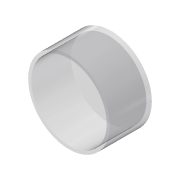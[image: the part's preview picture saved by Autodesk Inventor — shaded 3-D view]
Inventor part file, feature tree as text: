
AUTODESK INVENTOR PART (.ipt)
format: ipt  version: 2019.4 (Build 234330000, 330)  size: 91,136 bytes
history: native  units: mm
features: extrude x2, sketch x2, projected_geometry x1
ambient origin geometry x8: Origin, YZ Plane, XZ Plane, XY Plane, X Axis, Y Axis, Z Axis, Center Point
bodies: Solid1 (feature_tree)
feature tree (5):
  extrude  "Extrusion1"  Depth=18.0mm TaperAngle=0.0deg
  extrude  "Extrusion2"  [1 undecoded]
  sketch  "Sketch1"  dims[d0=35.0mm d1=18.0mm d2=0.0mm]
  sketch  "Sketch2"  dims[d3=17.0mm d4=0.0mm]
  projected_geometry  "Projected Loop1"
note: 1 required parameter value undecoded (feature->parameter linkage not recoverable at this tier; creation-order binding heuristic only, values carry confidence <= 0.55)
